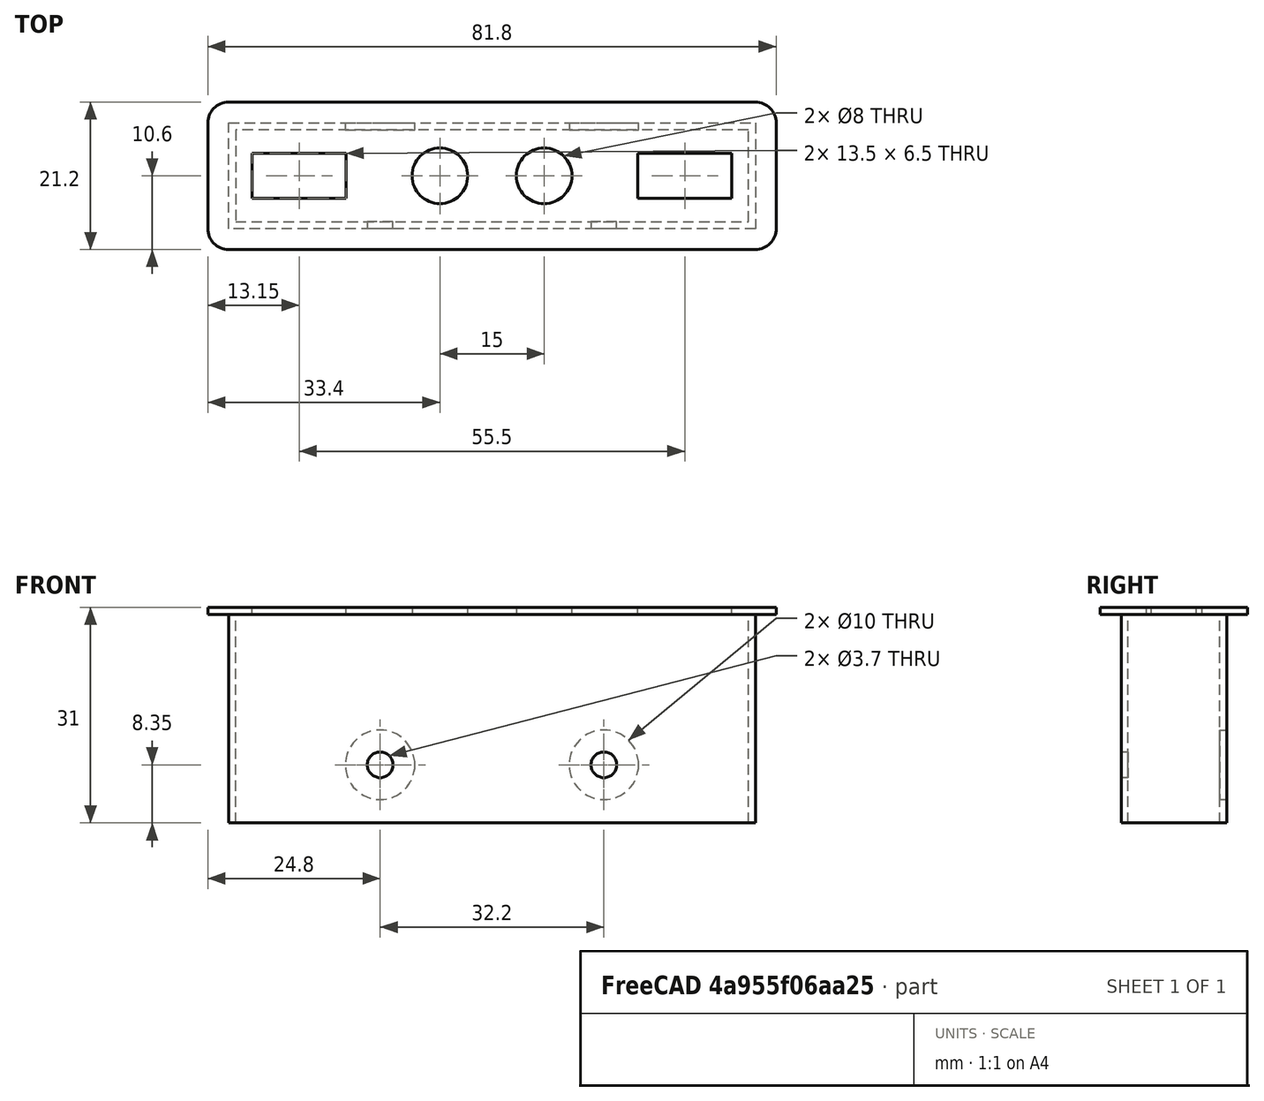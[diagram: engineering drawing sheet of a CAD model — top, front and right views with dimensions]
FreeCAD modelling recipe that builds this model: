
FCSTD DOCUMENT  (FreeCAD 0.18R13728 (Git))
Label: test114_frontio
License: All rights reserved
LicenseURL: http://en.wikipedia.org/wiki/All_rights_reserved
objects: Sketcher::SketchObject×4, PartDesign::Pad×2, PartDesign::Pocket×2, PartDesign::Body×1, Mesh::Feature×1
note: 13 computed .brp shape members not serialized (recipe doc carries the construction recipe); baked Part::Feature solids carry a one-line shape summary decoded from their .brp

FEATURE [Sketcher::SketchObject] Sketch
  MapMode = 5
  Support = -> [XY_Plane]
  sketch-geometry (8):
    g0: LineSegment StartX=-36.9 StartY=-6.6 StartZ=0 EndX=36.9 EndY=-6.6 EndZ=0
    g1: LineSegment StartX=36.9 StartY=-6.6 StartZ=0 EndX=36.9 EndY=6.6 EndZ=0
    g2: LineSegment StartX=36.9 StartY=6.6 StartZ=0 EndX=-36.9 EndY=6.6 EndZ=0
    g3: LineSegment StartX=-36.9 StartY=6.6 StartZ=0 EndX=-36.9 EndY=-6.6 EndZ=0
    g4: LineSegment StartX=-37.9 StartY=7.6 StartZ=0 EndX=37.9 EndY=7.6 EndZ=0
    g5: LineSegment StartX=37.9 StartY=7.6 StartZ=0 EndX=37.9 EndY=-7.6 EndZ=0
    g6: LineSegment StartX=37.9 StartY=-7.6 StartZ=0 EndX=-37.9 EndY=-7.6 EndZ=0
    g7: LineSegment StartX=-37.9 StartY=-7.6 StartZ=0 EndX=-37.9 EndY=7.6 EndZ=0
  constraints (22):
    c: Coincident(g0,g1)
    c: Coincident(g1,g2)
    c: Coincident(g2,g3)
    c: Coincident(g3,g0)
    c: Horizontal(g0)
    c: Horizontal(g2)
    c: Vertical(g1)
    c: Vertical(g3)
    c: Symmetric(g2,g0,g-1)
    c: Distance(g3) = 13.2
    c: Distance(g2) = 73.8
    c: Coincident(g4,g5)
    c: Coincident(g5,g6)
    c: Coincident(g6,g7)
    c: Coincident(g7,g4)
    c: Horizontal(g4)
    c: Horizontal(g6)
    c: Vertical(g5)
    c: Vertical(g7)
    c: Symmetric(g7,g5,g-1)
    c: Distance(g1,g5) = 1
    c: Distance(g2,g4) = 1
FEATURE [PartDesign::Pad] Pad
  Length = 30
  Length2 = 100
  Profile = -> Sketch
  Type = 0
FEATURE [Sketcher::SketchObject] Sketch001
  ExternalGeometry = -> [Pad]
  MapMode = 5
  Placement = pos=(0,-7.6,0) rot=(1,0,0;1.5708rad)
  Support = -> [Pad]
  sketch-geometry (10):
    g0: Circle CenterX=-16.1 CenterY=8.35 CenterZ=0 NormalX=0 NormalY=0 NormalZ=1 AngleXU=0 Radius=1.85
    g1: LineSegment [constr] StartX=-17.95 StartY=10.2 StartZ=0 EndX=-14.25 EndY=10.2 EndZ=0
    g2: LineSegment [constr] StartX=-14.25 StartY=10.2 StartZ=0 EndX=-14.25 EndY=6.5 EndZ=0
    g3: LineSegment [constr] StartX=-14.25 StartY=6.5 StartZ=0 EndX=-17.95 EndY=6.5 EndZ=0
    g4: LineSegment [constr] StartX=-17.95 StartY=6.5 StartZ=0 EndX=-17.95 EndY=10.2 EndZ=0
    g5: Circle CenterX=16.1 CenterY=8.35 CenterZ=0 NormalX=0 NormalY=0 NormalZ=1 AngleXU=0 Radius=1.85
    g6: LineSegment [constr] StartX=14.25 StartY=10.2 StartZ=0 EndX=17.95 EndY=10.2 EndZ=0
    g7: LineSegment [constr] StartX=17.95 StartY=10.2 StartZ=0 EndX=17.95 EndY=6.5 EndZ=0
    g8: LineSegment [constr] StartX=17.95 StartY=6.5 StartZ=0 EndX=14.25 EndY=6.5 EndZ=0
    g9: LineSegment [constr] StartX=14.25 StartY=6.5 StartZ=0 EndX=14.25 EndY=10.2 EndZ=0
  constraints (27):
    c: Radius(g0) = 1.85
    c: Coincident(g1,g2)
    c: Coincident(g2,g3)
    c: Coincident(g3,g4)
    c: Coincident(g4,g1)
    c: Horizontal(g1)
    c: Horizontal(g3)
    c: Vertical(g2)
    c: Vertical(g4)
    c: Equal(g1,g2)
    c: Symmetric(g1,g2,g0)
    c: Tangent(g2,g0)
    c: Distance(g1,g-3) = 19.8
    c: Distance(g1,g-4) = 19.95
    c: Radius(g5) = 1.85
    c: Coincident(g6,g7)
    c: Coincident(g7,g8)
    c: Coincident(g8,g9)
    c: Coincident(g9,g6)
    c: Horizontal(g6)
    c: Horizontal(g8)
    c: Vertical(g7)
    c: Vertical(g9)
    c: Equal(g6,g7)
    c: Symmetric(g6,g7,g5)
    c: Tangent(g7,g5)
    c: Symmetric(g0,g5,g-2)
FEATURE [PartDesign::Pocket] Pocket
  BaseFeature = -> Pad
  Length = 2
  Length2 = 100
  Profile = -> Sketch001
  Type = 0
FEATURE [Sketcher::SketchObject] Sketch002
  ExternalGeometry = -> [Pocket]
  MapMode = 5
  Placement = pos=(0,7.6,0) rot=(0,0.707107,0.707107;3.14159rad)
  Support = -> [Pocket]
  sketch-geometry (2):
    g0: Circle CenterX=-16.1 CenterY=8.35 CenterZ=0 NormalX=0 NormalY=0 NormalZ=1 AngleXU=0 Radius=5
    g1: Circle CenterX=16.1 CenterY=8.35 CenterZ=0 NormalX=0 NormalY=0 NormalZ=1 AngleXU=0 Radius=5
  constraints (4):
    c: Coincident(g0,g-3)
    c: Coincident(g1,g-4)
    c: Equal(g0,g1)
    c: Radius(g0) = 5
FEATURE [PartDesign::Pocket] Pocket001
  BaseFeature = -> Pocket
  Length = 2
  Length2 = 100
  Profile = -> Sketch002
  Type = 0
FEATURE [Sketcher::SketchObject] Sketch003
  ExternalGeometry = -> [Pocket001]
  MapMode = 5
  Placement = pos=(0,0,30) rot=(0,0,1;0rad)
  Support = -> [Pocket001]
  sketch-geometry (18):
    g0: LineSegment StartX=-34.5 StartY=-3.25 StartZ=0 EndX=-21 EndY=-3.25 EndZ=0
    g1: LineSegment StartX=-21 StartY=-3.25 StartZ=0 EndX=-21 EndY=3.25 EndZ=0
    g2: LineSegment StartX=-21 StartY=3.25 StartZ=0 EndX=-34.5 EndY=3.25 EndZ=0
    g3: LineSegment StartX=-34.5 StartY=3.25 StartZ=0 EndX=-34.5 EndY=-3.25 EndZ=0
    g4: LineSegment StartX=21 StartY=-3.25 StartZ=0 EndX=34.5 EndY=-3.25 EndZ=0
    g5: LineSegment StartX=34.5 StartY=-3.25 StartZ=0 EndX=34.5 EndY=3.25 EndZ=0
    g6: LineSegment StartX=34.5 StartY=3.25 StartZ=0 EndX=21 EndY=3.25 EndZ=0
    g7: LineSegment StartX=21 StartY=3.25 StartZ=0 EndX=21 EndY=-3.25 EndZ=0
    g8: Circle CenterX=-7.5 CenterY=0 CenterZ=0 NormalX=0 NormalY=0 NormalZ=1 AngleXU=0 Radius=4
    g9: Circle CenterX=7.5 CenterY=0 CenterZ=0 NormalX=0 NormalY=0 NormalZ=1 AngleXU=0 Radius=4
    g10: LineSegment StartX=-37.9 StartY=10.6 StartZ=0 EndX=37.9 EndY=10.6 EndZ=0
    g11: LineSegment StartX=40.9 StartY=7.6 StartZ=0 EndX=40.9 EndY=-7.6 EndZ=0
    g12: LineSegment StartX=37.9 StartY=-10.6 StartZ=0 EndX=-37.9 EndY=-10.6 EndZ=0
    g13: LineSegment StartX=-40.9 StartY=-7.6 StartZ=0 EndX=-40.9 EndY=7.6 EndZ=0
    g14: ArcOfCircle CenterX=-37.9 CenterY=7.6 CenterZ=0 NormalX=0 NormalY=0 NormalZ=1 AngleXU=0 Radius=3 StartAngle=1.5708 EndAngle=3.14159
    g15: ArcOfCircle CenterX=37.9 CenterY=7.6 CenterZ=0 NormalX=0 NormalY=0 NormalZ=1 AngleXU=0 Radius=3 StartAngle=0 EndAngle=1.5708
    g16: ArcOfCircle CenterX=37.9 CenterY=-7.6 CenterZ=0 NormalX=0 NormalY=0 NormalZ=1 AngleXU=0 Radius=3 StartAngle=4.71239 EndAngle=6.28319
    g17: ArcOfCircle CenterX=-37.9 CenterY=-7.6 CenterZ=0 NormalX=0 NormalY=0 NormalZ=1 AngleXU=0 Radius=3 StartAngle=3.14159 EndAngle=4.71239
  constraints (45):
    c: Coincident(g0,g1)
    c: Coincident(g1,g2)
    c: Coincident(g2,g3)
    c: Coincident(g3,g0)
    c: Horizontal(g0)
    c: Horizontal(g2)
    c: Vertical(g1)
    c: Vertical(g3)
    c: Coincident(g4,g5)
    c: Coincident(g5,g6)
    c: Coincident(g6,g7)
    c: Coincident(g7,g4)
    c: Horizontal(g4)
    c: Horizontal(g6)
    c: Vertical(g5)
    c: Vertical(g7)
    c: Equal(g2,g6)
    c: Equal(g9,g8)
    c: Equal(g1,g7)
    c: Distance(g6) = 13.5
    c: Radius(g9) = 4
    c: Distance(g7) = 6.5
    c: PointOnObject(g8,g-1)
    c: PointOnObject(g9,g-1)
    c: Symmetric(g8,g9,g-2)
    c: Symmetric(g1,g6,g-2)
    c: Symmetric(g0,g1,g-1)
    c: Distance(g8,g9) = 15
    c: Distance(g1,g7) = 42
    c: Tangent(g13,g14) = 1.5708
    c: Tangent(g10,g14) = 1.5708
    c: Tangent(g10,g15) = 1.5708
    c: Tangent(g11,g15) = 1.5708
    c: Tangent(g11,g16) = 1.5708
    c: Tangent(g12,g16) = 1.5708
    c: Tangent(g12,g17) = 1.5708
    c: Tangent(g13,g17) = 1.5708
    c: Coincident(g17,g-7)
    c: Coincident(g14,g-6)
    c: Coincident(g-10,g15)
    c: Coincident(g16,g-10)
    c: Radius(g17) = 3
    c: Equal(g17,g14)
    c: Equal(g17,g15)
    c: Equal(g17,g16)
FEATURE [PartDesign::Pad] Pad001
  BaseFeature = -> Pocket001
  Length = 1
  Length2 = 100
  Profile = -> Sketch003
  Type = 0
FEATURE [PartDesign::Body] Body
  Group = -> [Sketch,Pad,Sketch001,Pocket,Sketch002,Pocket001,Sketch003,Pad001]
  Origin = -> Origin
  Tip = -> Pad001
FEATURE [Mesh::Feature] Mesh  label="Pad001 (Meshed)"
  Placement = pos=(0,0,0) rot=(0,1,0;3.14159rad)
